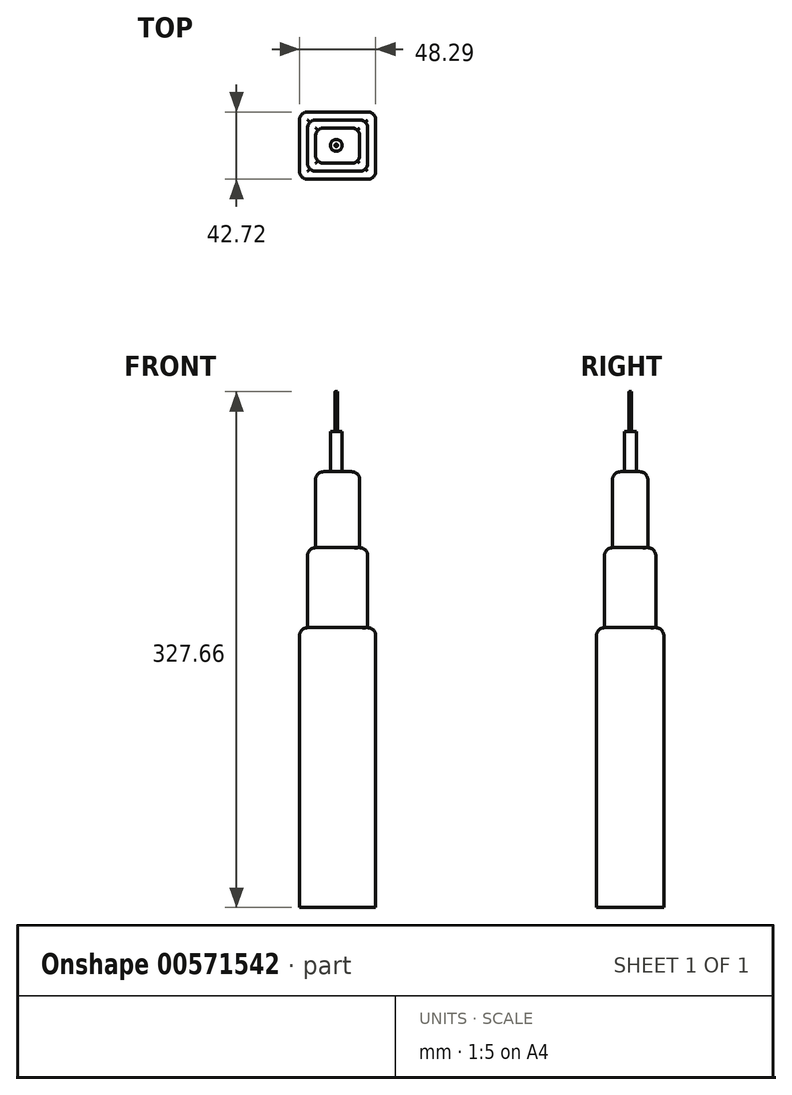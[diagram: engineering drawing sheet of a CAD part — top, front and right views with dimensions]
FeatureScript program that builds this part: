
annotation { "Feature Type Name" : "Feature", "Feature Type Description" : "" }
export const myFeature = defineFeature(function(context is Context, id is Id, definition is map)
    precondition{}
    {
        {
            var Q0;
            Q0=qCreatedBy(makeId("Top.planeOp"),FACE);
            var sketch = newSketch(context, id + "F0", { "sketchPlane" : qUnion([Q0])});
            skLineSegment(sketch, "E0.bottom", {"start": v(-66.74, 48.16) * mm, "end": v(-18.45, 48.16) * mm});
            skLineSegment(sketch, "E0.top", {"start": v(-66.74, 5.44) * mm, "end": v(-18.45, 5.44) * mm});
            skLineSegment(sketch, "E0.left", {"start": v(-66.74, 48.16) * mm, "end": v(-66.74, 5.44) * mm});
            skLineSegment(sketch, "E0.right", {"start": v(-18.45, 48.16) * mm, "end": v(-18.45, 5.44) * mm});
            skSolve(sketch);
        }
        {
            var Q0;
            Q0=makeQuery(id+"F0.imprint","IMPRINT",FACE,{"disambiguationData":[TD([[makeQuery(id+"F0.imprint","IMPRINT",EDGE,{"derivedFrom":sQuery(id+"F0.wireOp",EDGE,"E0.bottom")}),-1.0]])]});
            extrude(context, id + "F1", {"entities" : qUnion([Q0]), "depth" : 177.8 * mm, "offsetDistance" : 25.4 * mm});
        }
        {
            var Q0;
            Q0=makeQuery(id+"F1.opExtrude","SWEPT_EDGE",EDGE,{"disambiguationData":[OSD([sQuery(id+"F0.wireOp",EDGE,"E0.top"),sQuery(id+"F0.wireOp",EDGE,"E0.left")])]});
            var Q1;
            Q1=makeQuery(id+"F1.opExtrude","SWEPT_EDGE",EDGE,{"disambiguationData":[OSD([sQuery(id+"F0.wireOp",EDGE,"E0.top"),sQuery(id+"F0.wireOp",EDGE,"E0.right")])]});
            var Q2;
            Q2=makeQuery(id+"F1.opExtrude","CAP_EDGE",EDGE,{"disambiguationData":[OSD([sQuery(id+"F0.wireOp",EDGE,"E0.top")])],"isStart":false});
            var Q3;
            Q3=makeQuery(id+"F1.opExtrude","CAP_EDGE",EDGE,{"disambiguationData":[OSD([sQuery(id+"F0.wireOp",EDGE,"E0.bottom")])],"isStart":false});
            var Q4;
            Q4=makeQuery(id+"F1.opExtrude","SWEPT_EDGE",EDGE,{"disambiguationData":[OSD([sQuery(id+"F0.wireOp",EDGE,"E0.bottom"),sQuery(id+"F0.wireOp",EDGE,"E0.left")])]});
            var Q5;
            Q5=makeQuery(id+"F1.opExtrude","CAP_EDGE",EDGE,{"disambiguationData":[OSD([sQuery(id+"F0.wireOp",EDGE,"E0.left")])],"isStart":false});
            var Q6;
            Q6=makeQuery(id+"F1.opExtrude","CAP_EDGE",EDGE,{"disambiguationData":[OSD([sQuery(id+"F0.wireOp",EDGE,"E0.right")])],"isStart":false});
            var Q7;
            Q7=makeQuery(id+"F1.opExtrude","SWEPT_EDGE",EDGE,{"disambiguationData":[OSD([sQuery(id+"F0.wireOp",EDGE,"E0.bottom"),sQuery(id+"F0.wireOp",EDGE,"E0.right")])]});
            fillet(context, id + "F2", {"entities" : qUnion([Q0, Q1, Q2, Q3, Q4, Q5, Q6, Q7]), "radius" : 5.08 * mm, "tangentPropagation" : true, "allowEdgeOverflow" : false});
        }
        {
            var Q0;
            Q0=makeQuery(id+"F1.opExtrude","CAP_FACE",FACE,{"disambiguationData":[OSD([sQuery(id+"F0.wireOp",EDGE,"E0.bottom"),sQuery(id+"F0.wireOp",EDGE,"E0.top"),sQuery(id+"F0.wireOp",EDGE,"E0.left"),sQuery(id+"F0.wireOp",EDGE,"E0.right")])],"isStart":false});
            extrude(context, id + "F3", {"entities" : qUnion([Q0]), "operationType" : NewBodyOperationType.ADD, "depth" : 50.8 * mm, "offsetDistance" : 25.4 * mm});
        }
        {
            var Q0;
            {var subQ0=sQuery(id+"F0.wireOp",EDGE,"E0.right");var subQ1=sQuery(id+"F0.wireOp",EDGE,"E0.left");var subQ2=sQuery(id+"F0.wireOp",EDGE,"E0.top");var subQ3=sQuery(id+"F0.wireOp",EDGE,"E0.bottom");Q0=makeQuery(id+"F3.opExtrude","SWEPT_EDGE",EDGE,{"disambiguationData":[OSD([subQ3,subQ2,subQ1,subQ0]),TDD([makeQuery(id+"F2.opFillet","BLEND_VERTEX",VERTEX,{"blendedFrom":[makeQuery(id+"F1.opExtrude","CAP_VERTEX",VERTEX,{"disambiguationData":[OSD([subQ3,subQ0])],"isStart":false}),makeQuery(id+"F1.opExtrude","CAP_EDGE",EDGE,{"disambiguationData":[OSD([subQ3])],"isStart":false}),makeQuery(id+"F1.opExtrude","CAP_EDGE",EDGE,{"disambiguationData":[OSD([subQ0])],"isStart":false}),makeQuery(id+"F1.opExtrude","CAP_FACE",FACE,{"disambiguationData":[OSD([subQ3,subQ2,subQ1,subQ0])],"isStart":false})],"blendedInto":[makeQuery(id+"F1.opExtrude","CAP_FACE",FACE,{"disambiguationData":[OSD([subQ3,subQ2,subQ1,subQ0])],"isStart":false})]})])]});}
            var Q1;
            {var subQ0=sQuery(id+"F0.wireOp",EDGE,"E0.right");var subQ1=sQuery(id+"F0.wireOp",EDGE,"E0.left");var subQ2=sQuery(id+"F0.wireOp",EDGE,"E0.top");var subQ3=sQuery(id+"F0.wireOp",EDGE,"E0.bottom");Q1=makeQuery(id+"F3.opExtrude","CAP_EDGE",EDGE,{"disambiguationData":[OSD([subQ3,subQ2,subQ1,subQ0]),TDD([makeQuery(id+"F2.opFillet","BLEND_EDGE",EDGE,{"blendedFrom":[makeQuery(id+"F1.opExtrude","CAP_EDGE",EDGE,{"disambiguationData":[OSD([subQ3])],"isStart":false}),makeQuery(id+"F1.opExtrude","CAP_FACE",FACE,{"disambiguationData":[OSD([subQ3,subQ2,subQ1,subQ0])],"isStart":false})],"blendedInto":[makeQuery(id+"F1.opExtrude","CAP_FACE",FACE,{"disambiguationData":[OSD([subQ3,subQ2,subQ1,subQ0])],"isStart":false})]})])],"isStart":false});}
            var Q2;
            {var subQ0=sQuery(id+"F0.wireOp",EDGE,"E0.right");var subQ1=sQuery(id+"F0.wireOp",EDGE,"E0.left");var subQ2=sQuery(id+"F0.wireOp",EDGE,"E0.top");var subQ3=sQuery(id+"F0.wireOp",EDGE,"E0.bottom");Q2=makeQuery(id+"F3.opExtrude","CAP_EDGE",EDGE,{"disambiguationData":[OSD([subQ3,subQ2,subQ1,subQ0]),TDD([makeQuery(id+"F2.opFillet","BLEND_EDGE",EDGE,{"blendedFrom":[makeQuery(id+"F1.opExtrude","CAP_EDGE",EDGE,{"disambiguationData":[OSD([subQ0])],"isStart":false}),makeQuery(id+"F1.opExtrude","CAP_FACE",FACE,{"disambiguationData":[OSD([subQ3,subQ2,subQ1,subQ0])],"isStart":false})],"blendedInto":[makeQuery(id+"F1.opExtrude","CAP_FACE",FACE,{"disambiguationData":[OSD([subQ3,subQ2,subQ1,subQ0])],"isStart":false})]})])],"isStart":false});}
            var Q3;
            {var subQ0=sQuery(id+"F0.wireOp",EDGE,"E0.right");var subQ1=sQuery(id+"F0.wireOp",EDGE,"E0.left");var subQ2=sQuery(id+"F0.wireOp",EDGE,"E0.top");var subQ3=sQuery(id+"F0.wireOp",EDGE,"E0.bottom");Q3=makeQuery(id+"F3.opExtrude","SWEPT_EDGE",EDGE,{"disambiguationData":[OSD([subQ3,subQ2,subQ1,subQ0]),TDD([makeQuery(id+"F2.opFillet","BLEND_VERTEX",VERTEX,{"blendedFrom":[makeQuery(id+"F1.opExtrude","CAP_VERTEX",VERTEX,{"disambiguationData":[OSD([subQ2,subQ0])],"isStart":false}),makeQuery(id+"F1.opExtrude","CAP_EDGE",EDGE,{"disambiguationData":[OSD([subQ2])],"isStart":false}),makeQuery(id+"F1.opExtrude","CAP_EDGE",EDGE,{"disambiguationData":[OSD([subQ0])],"isStart":false}),makeQuery(id+"F1.opExtrude","CAP_FACE",FACE,{"disambiguationData":[OSD([subQ3,subQ2,subQ1,subQ0])],"isStart":false})],"blendedInto":[makeQuery(id+"F1.opExtrude","CAP_FACE",FACE,{"disambiguationData":[OSD([subQ3,subQ2,subQ1,subQ0])],"isStart":false})]})])]});}
            var Q4;
            {var subQ0=sQuery(id+"F0.wireOp",EDGE,"E0.right");var subQ1=sQuery(id+"F0.wireOp",EDGE,"E0.left");var subQ2=sQuery(id+"F0.wireOp",EDGE,"E0.top");var subQ3=sQuery(id+"F0.wireOp",EDGE,"E0.bottom");Q4=makeQuery(id+"F3.opExtrude","CAP_EDGE",EDGE,{"disambiguationData":[OSD([subQ3,subQ2,subQ1,subQ0]),TDD([makeQuery(id+"F2.opFillet","BLEND_EDGE",EDGE,{"blendedFrom":[makeQuery(id+"F1.opExtrude","CAP_EDGE",EDGE,{"disambiguationData":[OSD([subQ2])],"isStart":false}),makeQuery(id+"F1.opExtrude","CAP_FACE",FACE,{"disambiguationData":[OSD([subQ3,subQ2,subQ1,subQ0])],"isStart":false})],"blendedInto":[makeQuery(id+"F1.opExtrude","CAP_FACE",FACE,{"disambiguationData":[OSD([subQ3,subQ2,subQ1,subQ0])],"isStart":false})]})])],"isStart":false});}
            var Q5;
            {var subQ0=sQuery(id+"F0.wireOp",EDGE,"E0.right");var subQ1=sQuery(id+"F0.wireOp",EDGE,"E0.left");var subQ2=sQuery(id+"F0.wireOp",EDGE,"E0.top");var subQ3=sQuery(id+"F0.wireOp",EDGE,"E0.bottom");Q5=makeQuery(id+"F3.opExtrude","CAP_EDGE",EDGE,{"disambiguationData":[OSD([subQ3,subQ2,subQ1,subQ0]),TDD([makeQuery(id+"F2.opFillet","BLEND_EDGE",EDGE,{"blendedFrom":[makeQuery(id+"F1.opExtrude","CAP_EDGE",EDGE,{"disambiguationData":[OSD([subQ1])],"isStart":false}),makeQuery(id+"F1.opExtrude","CAP_FACE",FACE,{"disambiguationData":[OSD([subQ3,subQ2,subQ1,subQ0])],"isStart":false})],"blendedInto":[makeQuery(id+"F1.opExtrude","CAP_FACE",FACE,{"disambiguationData":[OSD([subQ3,subQ2,subQ1,subQ0])],"isStart":false})]})])],"isStart":false});}
            var Q6;
            {var subQ0=sQuery(id+"F0.wireOp",EDGE,"E0.right");var subQ1=sQuery(id+"F0.wireOp",EDGE,"E0.left");var subQ2=sQuery(id+"F0.wireOp",EDGE,"E0.top");var subQ3=sQuery(id+"F0.wireOp",EDGE,"E0.bottom");Q6=makeQuery(id+"F3.opExtrude","SWEPT_EDGE",EDGE,{"disambiguationData":[OSD([subQ3,subQ2,subQ1,subQ0]),TDD([makeQuery(id+"F2.opFillet","BLEND_VERTEX",VERTEX,{"blendedFrom":[makeQuery(id+"F1.opExtrude","CAP_VERTEX",VERTEX,{"disambiguationData":[OSD([subQ3,subQ1])],"isStart":false}),makeQuery(id+"F1.opExtrude","CAP_EDGE",EDGE,{"disambiguationData":[OSD([subQ3])],"isStart":false}),makeQuery(id+"F1.opExtrude","CAP_EDGE",EDGE,{"disambiguationData":[OSD([subQ1])],"isStart":false}),makeQuery(id+"F1.opExtrude","CAP_FACE",FACE,{"disambiguationData":[OSD([subQ3,subQ2,subQ1,subQ0])],"isStart":false})],"blendedInto":[makeQuery(id+"F1.opExtrude","CAP_FACE",FACE,{"disambiguationData":[OSD([subQ3,subQ2,subQ1,subQ0])],"isStart":false})]})])]});}
            var Q7;
            {var subQ0=sQuery(id+"F0.wireOp",EDGE,"E0.right");var subQ1=sQuery(id+"F0.wireOp",EDGE,"E0.left");var subQ2=sQuery(id+"F0.wireOp",EDGE,"E0.top");var subQ3=sQuery(id+"F0.wireOp",EDGE,"E0.bottom");Q7=makeQuery(id+"F3.opExtrude","SWEPT_EDGE",EDGE,{"disambiguationData":[OSD([subQ3,subQ2,subQ1,subQ0]),TDD([makeQuery(id+"F2.opFillet","BLEND_VERTEX",VERTEX,{"blendedFrom":[makeQuery(id+"F1.opExtrude","CAP_VERTEX",VERTEX,{"disambiguationData":[OSD([subQ2,subQ1])],"isStart":false}),makeQuery(id+"F1.opExtrude","CAP_EDGE",EDGE,{"disambiguationData":[OSD([subQ2])],"isStart":false}),makeQuery(id+"F1.opExtrude","CAP_EDGE",EDGE,{"disambiguationData":[OSD([subQ1])],"isStart":false}),makeQuery(id+"F1.opExtrude","CAP_FACE",FACE,{"disambiguationData":[OSD([subQ3,subQ2,subQ1,subQ0])],"isStart":false})],"blendedInto":[makeQuery(id+"F1.opExtrude","CAP_FACE",FACE,{"disambiguationData":[OSD([subQ3,subQ2,subQ1,subQ0])],"isStart":false})]})])]});}
            fillet(context, id + "F4", {"entities" : qUnion([Q0, Q1, Q2, Q3, Q4, Q5, Q6, Q7]), "radius" : 5.08 * mm, "tangentPropagation" : true, "allowEdgeOverflow" : false});
        }
        {
            var Q0;
            Q0=makeQuery(id+"F3.opExtrude","CAP_FACE",FACE,{"disambiguationData":[OSD([sQuery(id+"F0.wireOp",EDGE,"E0.bottom"),sQuery(id+"F0.wireOp",EDGE,"E0.top"),sQuery(id+"F0.wireOp",EDGE,"E0.left"),sQuery(id+"F0.wireOp",EDGE,"E0.right")])],"isStart":false});
            extrude(context, id + "F5", {"entities" : qUnion([Q0]), "operationType" : NewBodyOperationType.ADD, "depth" : 48.26 * mm, "offsetDistance" : 25.4 * mm});
        }
        {
            var Q0;
            {var subQ0=sQuery(id+"F0.wireOp",EDGE,"E0.right");var subQ1=sQuery(id+"F0.wireOp",EDGE,"E0.left");var subQ2=sQuery(id+"F0.wireOp",EDGE,"E0.top");var subQ3=sQuery(id+"F0.wireOp",EDGE,"E0.bottom");var subQ4=makeQuery(id+"F1.opExtrude","CAP_FACE",FACE,{"disambiguationData":[OSD([subQ3,subQ2,subQ1,subQ0])],"isStart":false});var subQ5=makeQuery(id+"F1.opExtrude","CAP_EDGE",EDGE,{"disambiguationData":[OSD([subQ1])],"isStart":false});var subQ6=makeQuery(id+"F1.opExtrude","CAP_EDGE",EDGE,{"disambiguationData":[OSD([subQ3])],"isStart":false});Q0=makeQuery(id+"F5.opExtrude","SWEPT_EDGE",EDGE,{"disambiguationData":[OSD([subQ3,subQ2,subQ1,subQ0]),TDD([makeQuery(id+"F4.opFillet","BLEND_VERTEX",VERTEX,{"blendedFrom":[makeQuery(id+"F3.opExtrude","CAP_VERTEX",VERTEX,{"disambiguationData":[OSD([subQ3,subQ2,subQ1,subQ0]),TDD([makeQuery(id+"F2.opFillet","BLEND_VERTEX",VERTEX,{"blendedFrom":[makeQuery(id+"F1.opExtrude","CAP_VERTEX",VERTEX,{"disambiguationData":[OSD([subQ3,subQ1])],"isStart":false}),subQ6,subQ5,subQ4],"blendedInto":[subQ4]})])],"isStart":false}),makeQuery(id+"F3.opExtrude","CAP_EDGE",EDGE,{"disambiguationData":[OSD([subQ3,subQ2,subQ1,subQ0]),TDD([makeQuery(id+"F2.opFillet","BLEND_EDGE",EDGE,{"blendedFrom":[subQ6,subQ4],"blendedInto":[subQ4]})])],"isStart":false}),makeQuery(id+"F3.opExtrude","CAP_EDGE",EDGE,{"disambiguationData":[OSD([subQ3,subQ2,subQ1,subQ0]),TDD([makeQuery(id+"F2.opFillet","BLEND_EDGE",EDGE,{"blendedFrom":[subQ5,subQ4],"blendedInto":[subQ4]})])],"isStart":false}),makeQuery(id+"F3.opExtrude","CAP_FACE",FACE,{"disambiguationData":[OSD([subQ3,subQ2,subQ1,subQ0])],"isStart":false})],"blendedInto":[makeQuery(id+"F3.opExtrude","CAP_FACE",FACE,{"disambiguationData":[OSD([subQ3,subQ2,subQ1,subQ0])],"isStart":false})]})])]});}
            var Q1;
            {var subQ0=sQuery(id+"F0.wireOp",EDGE,"E0.right");var subQ1=sQuery(id+"F0.wireOp",EDGE,"E0.left");var subQ2=sQuery(id+"F0.wireOp",EDGE,"E0.top");var subQ3=sQuery(id+"F0.wireOp",EDGE,"E0.bottom");var subQ4=makeQuery(id+"F1.opExtrude","CAP_FACE",FACE,{"disambiguationData":[OSD([subQ3,subQ2,subQ1,subQ0])],"isStart":false});var subQ5=makeQuery(id+"F1.opExtrude","CAP_EDGE",EDGE,{"disambiguationData":[OSD([subQ0])],"isStart":false});var subQ6=makeQuery(id+"F1.opExtrude","CAP_EDGE",EDGE,{"disambiguationData":[OSD([subQ3])],"isStart":false});Q1=makeQuery(id+"F5.opExtrude","SWEPT_EDGE",EDGE,{"disambiguationData":[OSD([subQ3,subQ2,subQ1,subQ0]),TDD([makeQuery(id+"F4.opFillet","BLEND_VERTEX",VERTEX,{"blendedFrom":[makeQuery(id+"F3.opExtrude","CAP_VERTEX",VERTEX,{"disambiguationData":[OSD([subQ3,subQ2,subQ1,subQ0]),TDD([makeQuery(id+"F2.opFillet","BLEND_VERTEX",VERTEX,{"blendedFrom":[makeQuery(id+"F1.opExtrude","CAP_VERTEX",VERTEX,{"disambiguationData":[OSD([subQ3,subQ0])],"isStart":false}),subQ6,subQ5,subQ4],"blendedInto":[subQ4]})])],"isStart":false}),makeQuery(id+"F3.opExtrude","CAP_EDGE",EDGE,{"disambiguationData":[OSD([subQ3,subQ2,subQ1,subQ0]),TDD([makeQuery(id+"F2.opFillet","BLEND_EDGE",EDGE,{"blendedFrom":[subQ6,subQ4],"blendedInto":[subQ4]})])],"isStart":false}),makeQuery(id+"F3.opExtrude","CAP_EDGE",EDGE,{"disambiguationData":[OSD([subQ3,subQ2,subQ1,subQ0]),TDD([makeQuery(id+"F2.opFillet","BLEND_EDGE",EDGE,{"blendedFrom":[subQ5,subQ4],"blendedInto":[subQ4]})])],"isStart":false}),makeQuery(id+"F3.opExtrude","CAP_FACE",FACE,{"disambiguationData":[OSD([subQ3,subQ2,subQ1,subQ0])],"isStart":false})],"blendedInto":[makeQuery(id+"F3.opExtrude","CAP_FACE",FACE,{"disambiguationData":[OSD([subQ3,subQ2,subQ1,subQ0])],"isStart":false})]})])]});}
            var Q2;
            {var subQ0=sQuery(id+"F0.wireOp",EDGE,"E0.right");var subQ1=sQuery(id+"F0.wireOp",EDGE,"E0.left");var subQ2=sQuery(id+"F0.wireOp",EDGE,"E0.top");var subQ3=sQuery(id+"F0.wireOp",EDGE,"E0.bottom");Q2=makeQuery(id+"F5.opExtrude","CAP_EDGE",EDGE,{"disambiguationData":[OSD([subQ3,subQ2,subQ1,subQ0]),TDD([makeQuery(id+"F4.opFillet","BLEND_EDGE",EDGE,{"blendedFrom":[makeQuery(id+"F3.opExtrude","CAP_EDGE",EDGE,{"disambiguationData":[OSD([subQ3,subQ2,subQ1,subQ0]),TDD([makeQuery(id+"F2.opFillet","BLEND_EDGE",EDGE,{"blendedFrom":[makeQuery(id+"F1.opExtrude","CAP_EDGE",EDGE,{"disambiguationData":[OSD([subQ3])],"isStart":false}),makeQuery(id+"F1.opExtrude","CAP_FACE",FACE,{"disambiguationData":[OSD([subQ3,subQ2,subQ1,subQ0])],"isStart":false})],"blendedInto":[makeQuery(id+"F1.opExtrude","CAP_FACE",FACE,{"disambiguationData":[OSD([subQ3,subQ2,subQ1,subQ0])],"isStart":false})]})])],"isStart":false}),makeQuery(id+"F3.opExtrude","CAP_FACE",FACE,{"disambiguationData":[OSD([subQ3,subQ2,subQ1,subQ0])],"isStart":false})],"blendedInto":[makeQuery(id+"F3.opExtrude","CAP_FACE",FACE,{"disambiguationData":[OSD([subQ3,subQ2,subQ1,subQ0])],"isStart":false})]})])],"isStart":false});}
            var Q3;
            {var subQ0=sQuery(id+"F0.wireOp",EDGE,"E0.right");var subQ1=sQuery(id+"F0.wireOp",EDGE,"E0.left");var subQ2=sQuery(id+"F0.wireOp",EDGE,"E0.top");var subQ3=sQuery(id+"F0.wireOp",EDGE,"E0.bottom");Q3=makeQuery(id+"F5.opExtrude","CAP_EDGE",EDGE,{"disambiguationData":[OSD([subQ3,subQ2,subQ1,subQ0]),TDD([makeQuery(id+"F4.opFillet","BLEND_EDGE",EDGE,{"blendedFrom":[makeQuery(id+"F3.opExtrude","CAP_EDGE",EDGE,{"disambiguationData":[OSD([subQ3,subQ2,subQ1,subQ0]),TDD([makeQuery(id+"F2.opFillet","BLEND_EDGE",EDGE,{"blendedFrom":[makeQuery(id+"F1.opExtrude","CAP_EDGE",EDGE,{"disambiguationData":[OSD([subQ0])],"isStart":false}),makeQuery(id+"F1.opExtrude","CAP_FACE",FACE,{"disambiguationData":[OSD([subQ3,subQ2,subQ1,subQ0])],"isStart":false})],"blendedInto":[makeQuery(id+"F1.opExtrude","CAP_FACE",FACE,{"disambiguationData":[OSD([subQ3,subQ2,subQ1,subQ0])],"isStart":false})]})])],"isStart":false}),makeQuery(id+"F3.opExtrude","CAP_FACE",FACE,{"disambiguationData":[OSD([subQ3,subQ2,subQ1,subQ0])],"isStart":false})],"blendedInto":[makeQuery(id+"F3.opExtrude","CAP_FACE",FACE,{"disambiguationData":[OSD([subQ3,subQ2,subQ1,subQ0])],"isStart":false})]})])],"isStart":false});}
            var Q4;
            {var subQ0=sQuery(id+"F0.wireOp",EDGE,"E0.right");var subQ1=sQuery(id+"F0.wireOp",EDGE,"E0.left");var subQ2=sQuery(id+"F0.wireOp",EDGE,"E0.top");var subQ3=sQuery(id+"F0.wireOp",EDGE,"E0.bottom");Q4=makeQuery(id+"F5.opExtrude","CAP_EDGE",EDGE,{"disambiguationData":[OSD([subQ3,subQ2,subQ1,subQ0]),TDD([makeQuery(id+"F4.opFillet","BLEND_EDGE",EDGE,{"blendedFrom":[makeQuery(id+"F3.opExtrude","CAP_EDGE",EDGE,{"disambiguationData":[OSD([subQ3,subQ2,subQ1,subQ0]),TDD([makeQuery(id+"F2.opFillet","BLEND_EDGE",EDGE,{"blendedFrom":[makeQuery(id+"F1.opExtrude","CAP_EDGE",EDGE,{"disambiguationData":[OSD([subQ2])],"isStart":false}),makeQuery(id+"F1.opExtrude","CAP_FACE",FACE,{"disambiguationData":[OSD([subQ3,subQ2,subQ1,subQ0])],"isStart":false})],"blendedInto":[makeQuery(id+"F1.opExtrude","CAP_FACE",FACE,{"disambiguationData":[OSD([subQ3,subQ2,subQ1,subQ0])],"isStart":false})]})])],"isStart":false}),makeQuery(id+"F3.opExtrude","CAP_FACE",FACE,{"disambiguationData":[OSD([subQ3,subQ2,subQ1,subQ0])],"isStart":false})],"blendedInto":[makeQuery(id+"F3.opExtrude","CAP_FACE",FACE,{"disambiguationData":[OSD([subQ3,subQ2,subQ1,subQ0])],"isStart":false})]})])],"isStart":false});}
            var Q5;
            {var subQ0=sQuery(id+"F0.wireOp",EDGE,"E0.right");var subQ1=sQuery(id+"F0.wireOp",EDGE,"E0.left");var subQ2=sQuery(id+"F0.wireOp",EDGE,"E0.top");var subQ3=sQuery(id+"F0.wireOp",EDGE,"E0.bottom");var subQ4=makeQuery(id+"F1.opExtrude","CAP_FACE",FACE,{"disambiguationData":[OSD([subQ3,subQ2,subQ1,subQ0])],"isStart":false});var subQ5=makeQuery(id+"F1.opExtrude","CAP_EDGE",EDGE,{"disambiguationData":[OSD([subQ1])],"isStart":false});var subQ6=makeQuery(id+"F1.opExtrude","CAP_EDGE",EDGE,{"disambiguationData":[OSD([subQ2])],"isStart":false});Q5=makeQuery(id+"F5.opExtrude","SWEPT_EDGE",EDGE,{"disambiguationData":[OSD([subQ3,subQ2,subQ1,subQ0]),TDD([makeQuery(id+"F4.opFillet","BLEND_VERTEX",VERTEX,{"blendedFrom":[makeQuery(id+"F3.opExtrude","CAP_VERTEX",VERTEX,{"disambiguationData":[OSD([subQ3,subQ2,subQ1,subQ0]),TDD([makeQuery(id+"F2.opFillet","BLEND_VERTEX",VERTEX,{"blendedFrom":[makeQuery(id+"F1.opExtrude","CAP_VERTEX",VERTEX,{"disambiguationData":[OSD([subQ2,subQ1])],"isStart":false}),subQ6,subQ5,subQ4],"blendedInto":[subQ4]})])],"isStart":false}),makeQuery(id+"F3.opExtrude","CAP_EDGE",EDGE,{"disambiguationData":[OSD([subQ3,subQ2,subQ1,subQ0]),TDD([makeQuery(id+"F2.opFillet","BLEND_EDGE",EDGE,{"blendedFrom":[subQ6,subQ4],"blendedInto":[subQ4]})])],"isStart":false}),makeQuery(id+"F3.opExtrude","CAP_EDGE",EDGE,{"disambiguationData":[OSD([subQ3,subQ2,subQ1,subQ0]),TDD([makeQuery(id+"F2.opFillet","BLEND_EDGE",EDGE,{"blendedFrom":[subQ5,subQ4],"blendedInto":[subQ4]})])],"isStart":false}),makeQuery(id+"F3.opExtrude","CAP_FACE",FACE,{"disambiguationData":[OSD([subQ3,subQ2,subQ1,subQ0])],"isStart":false})],"blendedInto":[makeQuery(id+"F3.opExtrude","CAP_FACE",FACE,{"disambiguationData":[OSD([subQ3,subQ2,subQ1,subQ0])],"isStart":false})]})])]});}
            var Q6;
            {var subQ0=sQuery(id+"F0.wireOp",EDGE,"E0.right");var subQ1=sQuery(id+"F0.wireOp",EDGE,"E0.left");var subQ2=sQuery(id+"F0.wireOp",EDGE,"E0.top");var subQ3=sQuery(id+"F0.wireOp",EDGE,"E0.bottom");Q6=makeQuery(id+"F5.opExtrude","CAP_EDGE",EDGE,{"disambiguationData":[OSD([subQ3,subQ2,subQ1,subQ0]),TDD([makeQuery(id+"F4.opFillet","BLEND_EDGE",EDGE,{"blendedFrom":[makeQuery(id+"F3.opExtrude","CAP_EDGE",EDGE,{"disambiguationData":[OSD([subQ3,subQ2,subQ1,subQ0]),TDD([makeQuery(id+"F2.opFillet","BLEND_EDGE",EDGE,{"blendedFrom":[makeQuery(id+"F1.opExtrude","CAP_EDGE",EDGE,{"disambiguationData":[OSD([subQ1])],"isStart":false}),makeQuery(id+"F1.opExtrude","CAP_FACE",FACE,{"disambiguationData":[OSD([subQ3,subQ2,subQ1,subQ0])],"isStart":false})],"blendedInto":[makeQuery(id+"F1.opExtrude","CAP_FACE",FACE,{"disambiguationData":[OSD([subQ3,subQ2,subQ1,subQ0])],"isStart":false})]})])],"isStart":false}),makeQuery(id+"F3.opExtrude","CAP_FACE",FACE,{"disambiguationData":[OSD([subQ3,subQ2,subQ1,subQ0])],"isStart":false})],"blendedInto":[makeQuery(id+"F3.opExtrude","CAP_FACE",FACE,{"disambiguationData":[OSD([subQ3,subQ2,subQ1,subQ0])],"isStart":false})]})])],"isStart":false});}
            var Q7;
            {var subQ0=sQuery(id+"F0.wireOp",EDGE,"E0.right");var subQ1=sQuery(id+"F0.wireOp",EDGE,"E0.left");var subQ2=sQuery(id+"F0.wireOp",EDGE,"E0.top");var subQ3=sQuery(id+"F0.wireOp",EDGE,"E0.bottom");var subQ4=makeQuery(id+"F1.opExtrude","CAP_FACE",FACE,{"disambiguationData":[OSD([subQ3,subQ2,subQ1,subQ0])],"isStart":false});var subQ5=makeQuery(id+"F1.opExtrude","CAP_EDGE",EDGE,{"disambiguationData":[OSD([subQ0])],"isStart":false});var subQ6=makeQuery(id+"F1.opExtrude","CAP_EDGE",EDGE,{"disambiguationData":[OSD([subQ2])],"isStart":false});Q7=makeQuery(id+"F5.opExtrude","SWEPT_EDGE",EDGE,{"disambiguationData":[OSD([subQ3,subQ2,subQ1,subQ0]),TDD([makeQuery(id+"F4.opFillet","BLEND_VERTEX",VERTEX,{"blendedFrom":[makeQuery(id+"F3.opExtrude","CAP_VERTEX",VERTEX,{"disambiguationData":[OSD([subQ3,subQ2,subQ1,subQ0]),TDD([makeQuery(id+"F2.opFillet","BLEND_VERTEX",VERTEX,{"blendedFrom":[makeQuery(id+"F1.opExtrude","CAP_VERTEX",VERTEX,{"disambiguationData":[OSD([subQ2,subQ0])],"isStart":false}),subQ6,subQ5,subQ4],"blendedInto":[subQ4]})])],"isStart":false}),makeQuery(id+"F3.opExtrude","CAP_EDGE",EDGE,{"disambiguationData":[OSD([subQ3,subQ2,subQ1,subQ0]),TDD([makeQuery(id+"F2.opFillet","BLEND_EDGE",EDGE,{"blendedFrom":[subQ6,subQ4],"blendedInto":[subQ4]})])],"isStart":false}),makeQuery(id+"F3.opExtrude","CAP_EDGE",EDGE,{"disambiguationData":[OSD([subQ3,subQ2,subQ1,subQ0]),TDD([makeQuery(id+"F2.opFillet","BLEND_EDGE",EDGE,{"blendedFrom":[subQ5,subQ4],"blendedInto":[subQ4]})])],"isStart":false}),makeQuery(id+"F3.opExtrude","CAP_FACE",FACE,{"disambiguationData":[OSD([subQ3,subQ2,subQ1,subQ0])],"isStart":false})],"blendedInto":[makeQuery(id+"F3.opExtrude","CAP_FACE",FACE,{"disambiguationData":[OSD([subQ3,subQ2,subQ1,subQ0])],"isStart":false})]})])]});}
            fillet(context, id + "F6", {"entities" : qUnion([Q0, Q1, Q2, Q3, Q4, Q5, Q6, Q7]), "radius" : 5.08 * mm, "tangentPropagation" : true, "allowEdgeOverflow" : false});
        }
        {
            var Q0;
            Q0=makeQuery(id+"F5.opExtrude","CAP_FACE",FACE,{"disambiguationData":[OSD([sQuery(id+"F0.wireOp",EDGE,"E0.bottom"),sQuery(id+"F0.wireOp",EDGE,"E0.top"),sQuery(id+"F0.wireOp",EDGE,"E0.left"),sQuery(id+"F0.wireOp",EDGE,"E0.right")])],"isStart":false});
            var sketch = newSketch(context, id + "F7", { "sketchPlane" : qUnion([Q0])});
            skCircle(sketch, "E1", {"center": v(-43.48, 26.92) * mm, "radius": 3.76 * mm});
            skSolve(sketch);
        }
        {
            var Q0;
            Q0=makeQuery(id+"F7.imprint","IMPRINT",FACE,{"disambiguationData":[TD([[makeQuery(id+"F7.imprint","IMPRINT",EDGE,{"derivedFrom":sQuery(id+"F7.wireOp",EDGE,"E1")}),1.0]])]});
            extrude(context, id + "F8", {"entities" : qUnion([Q0]), "operationType" : NewBodyOperationType.ADD, "depth" : 25.4 * mm, "offsetDistance" : 25.4 * mm});
        }
        {
            var Q0;
            Q0=makeQuery(id+"F8.opExtrude","CAP_FACE",FACE,{"disambiguationData":[OSD([sQuery(id+"F7.wireOp",EDGE,"E1")])],"isStart":false});
            var sketch = newSketch(context, id + "F9", { "sketchPlane" : qUnion([Q0])});
            skCircle(sketch, "E2", {"center": v(-43.48, 26.92) * mm, "radius": 0.84 * mm});
            skSolve(sketch);
        }
        {
            var Q0;
            Q0=makeQuery(id+"F9.imprint","IMPRINT",FACE,{"disambiguationData":[TD([[makeQuery(id+"F9.imprint","IMPRINT",EDGE,{"derivedFrom":sQuery(id+"F9.wireOp",EDGE,"E2")}),1.0]])]});
            extrude(context, id + "F10", {"entities" : qUnion([Q0]), "operationType" : NewBodyOperationType.ADD, "depth" : 25.4 * mm, "offsetDistance" : 25.4 * mm});
        }
    });
